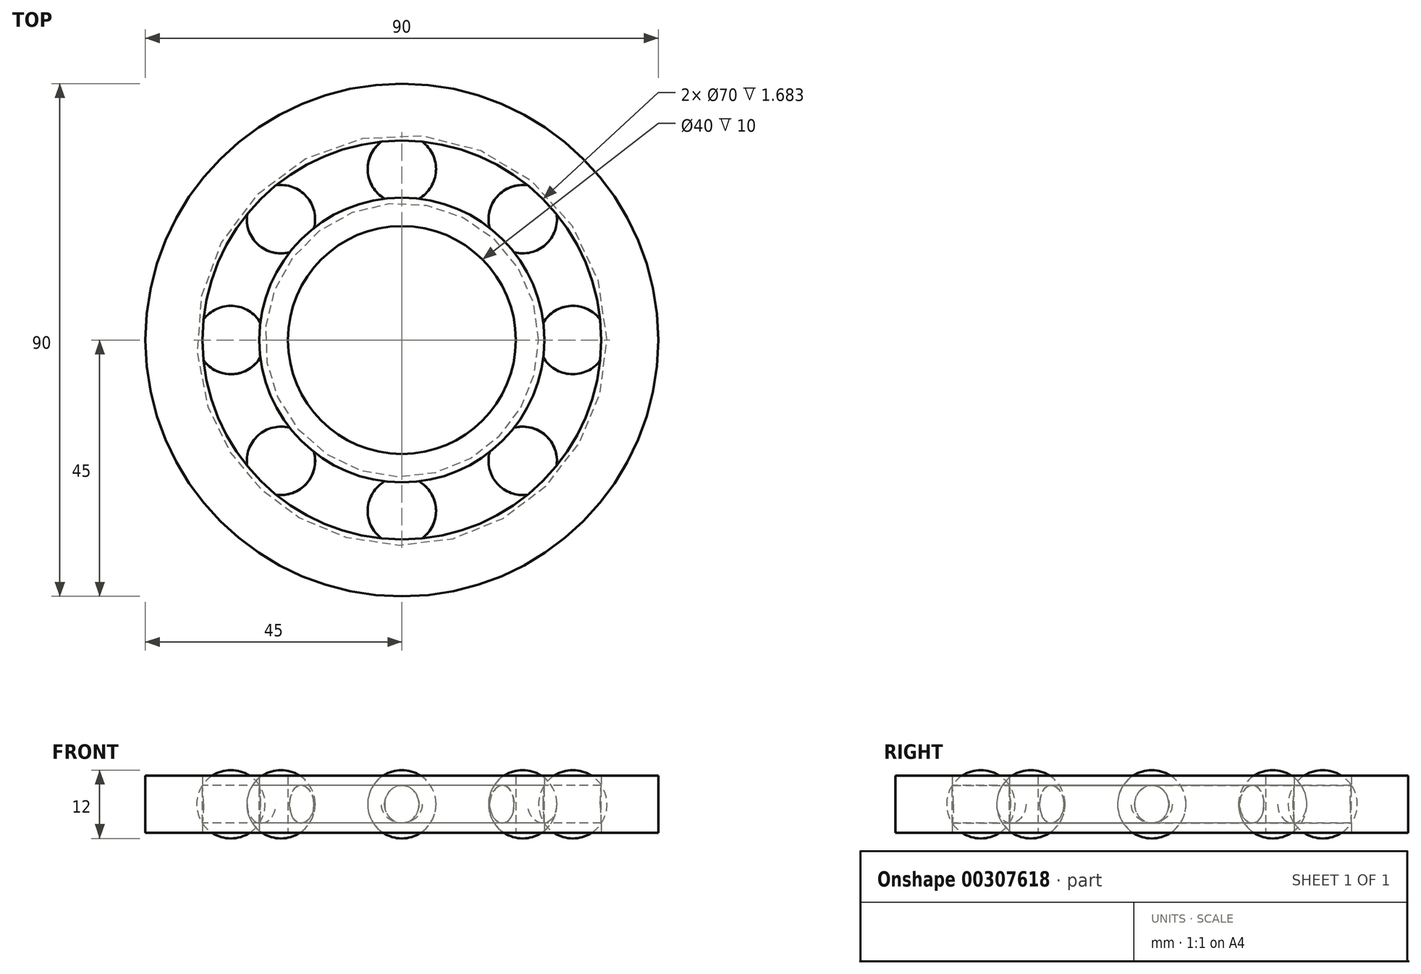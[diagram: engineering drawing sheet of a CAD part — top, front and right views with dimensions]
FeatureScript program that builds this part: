
annotation { "Feature Type Name" : "Feature", "Feature Type Description" : "" }
export const myFeature = defineFeature(function(context is Context, id is Id, definition is map)
    precondition{}
    {
        {
            var Q0;
            Q0=qCreatedBy(makeId("Top.planeOp"),FACE);
            var sketch = newSketch(context, id + "F0", { "sketchPlane" : qUnion([Q0])});
            skCircle(sketch, "E0", {"center": v(0, 0) * mm, "radius": 25 * mm});
            skCircle(sketch, "E1", {"center": v(0, 0) * mm, "radius": 35 * mm});
            skCircle(sketch, "E2", {"center": v(0, 30) * mm, "radius": 6 * mm, "construction": true});
            skLineSegment(sketch, "E3", {"start": v(0, 25) * mm, "end": v(0, 24) * mm, "construction": true});
            skLineSegment(sketch, "E4", {"start": v(0, 36) * mm, "end": v(0, 35) * mm, "construction": true});
            skCircle(sketch, "E5", {"center": v(0, 0) * mm, "radius": 45 * mm});
            skCircle(sketch, "E6", {"center": v(0, 0) * mm, "radius": 20 * mm});
            skSolve(sketch);
        }
        {
            var Q0;
            Q0=qCreatedBy(makeId("Top.planeOp"),FACE);
            var sketch = newSketch(context, id + "F1", { "sketchPlane" : qUnion([Q0])});
            skLineSegment(sketch, "E7", {"start": v(0, 24) * mm, "end": v(0, 36) * mm});
            skArc(sketch, "E8", {"start": v(0, 36) * mm, "mid": v(-6, 30) * mm, "end": v(0, 24) * mm});
            skSolve(sketch);
        }
        {
            var Q0;
            Q0=qSketchRegion(id+"F1",true);
            var Q1;
            Q1=sQuery(id+"F1.wireOp",EDGE,"E7");
            revolve(context, id + "F2", {"entities" : qUnion([Q0]), "axis" : qUnion([Q1]), "revolveType" : RevolveType.FULL});
        }
        {
            var Q0;
            Q0=makeQuery(id+"F0.imprint","IMPRINT",FACE,{"disambiguationData":[TD([[makeQuery(id+"F0.imprint","IMPRINT",EDGE,{"derivedFrom":sQuery(id+"F0.wireOp",EDGE,"E1")}),-1.0]])]});
            var Q1;
            Q1=makeQuery(id+"F0.imprint","IMPRINT",FACE,{"disambiguationData":[TD([[makeQuery(id+"F0.imprint","IMPRINT",EDGE,{"derivedFrom":sQuery(id+"F0.wireOp",EDGE,"E0")}),1.0]])]});
            extrude(context, id + "F3", {"entities" : qUnion([Q0, Q1]), "endBound" : BoundingType.SYMMETRIC, "depth" : 10 * mm});
        }
        {
            var Q0;
            Q0=qCreatedBy(makeId("Right.planeOp"),FACE);
            var sketch = newSketch(context, id + "F4", { "sketchPlane" : qUnion([Q0])});
            skLineSegment(sketch, "E9", {"start": v(25, 5) * mm, "end": v(25, -5) * mm});
            skArc(sketch, "E10", {"start": v(25, 3.32) * mm, "mid": v(24, 0) * mm, "end": v(25, -3.32) * mm});
            skArc(sketch, "E11", {"start": v(25, -3.32) * mm, "mid": v(30, -6) * mm, "end": v(35, -3.32) * mm, "construction": true});
            skLineSegment(sketch, "E12", {"start": v(35, 5) * mm, "end": v(35, -5) * mm});
            skArc(sketch, "E13", {"start": v(35, 3.32) * mm, "mid": v(30, 6) * mm, "end": v(25, 3.32) * mm, "construction": true});
            skArc(sketch, "E14", {"start": v(35, -3.32) * mm, "mid": v(36, 0) * mm, "end": v(35, 3.32) * mm});
            skSolve(sketch);
        }
        {
            var Q0;
            Q0=qSketchRegion(id+"F4",true);
            var Q1;
            Q1=makeQuery(id+"F3.opExtrude","CAP_EDGE",EDGE,{"disambiguationData":[OSD([sQuery(id+"F0.wireOp",EDGE,"E6")])],"isStart":false});
            revolve(context, id + "F5", {"operationType" : NewBodyOperationType.REMOVE, "entities" : qUnion([Q0]), "axis" : qUnion([Q1]), "revolveType" : RevolveType.FULL, "oppositeDirection" : true});
        }
        {
            var Q0;
            Q0=makeQuery(id+"F2.opRevolve","SWEPT_BODY",BODY,{"disambiguationData":[OSD([sQuery(id+"F1.wireOp",EDGE,"E7"),sQuery(id+"F1.wireOp",EDGE,"E8")])]});
            var Q1;
            Q1=makeQuery(id+"F3.opExtrude","CAP_EDGE",EDGE,{"disambiguationData":[OSD([sQuery(id+"F0.wireOp",EDGE,"E6")])],"isStart":false});
            circularPattern(context, id + "F6", {"entities" : qUnion([Q0]), "axis" : qUnion([Q1]), "angle" : 360 * degree, "instanceCount" : 8, "equalSpace" : true});
        }
    });
